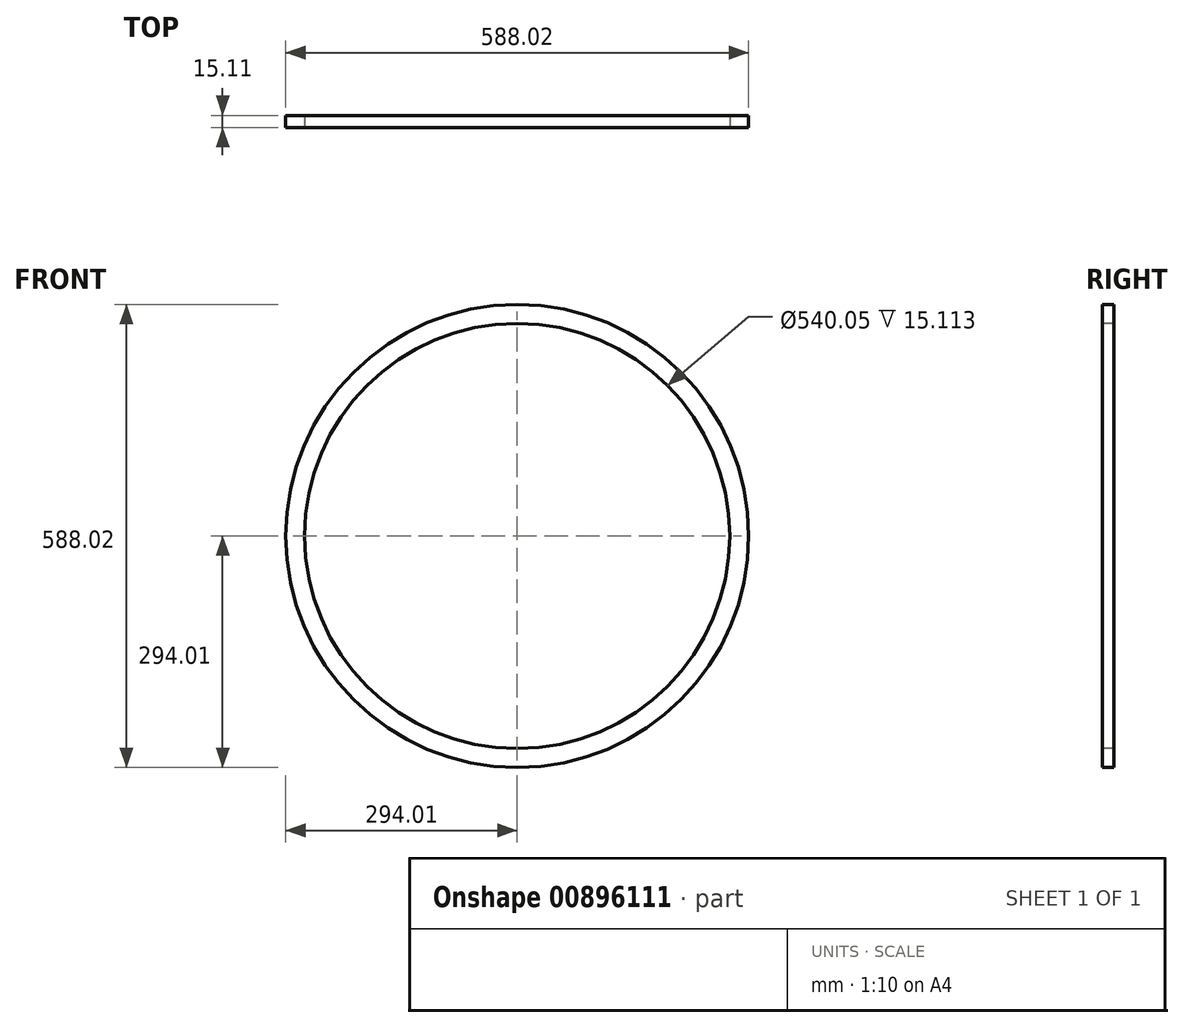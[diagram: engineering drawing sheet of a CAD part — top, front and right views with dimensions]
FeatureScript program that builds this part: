
annotation { "Feature Type Name" : "Feature", "Feature Type Description" : "" }
export const myFeature = defineFeature(function(context is Context, id is Id, definition is map)
    precondition{}
    {
        {
            var Q0;
            Q0=qCreatedBy(makeId("Front.planeOp"),FACE);
            var sketch = newSketch(context, id + "F0", { "sketchPlane" : qUnion([Q0])});
            skCircle(sketch, "E0", {"center": v(0, 0) * mm, "radius": 294 * mm});
            skCircle(sketch, "E1", {"center": v(0, 0) * mm, "radius": 270.03 * mm});
            skSolve(sketch);
        }
        {
            var Q0;
            Q0=makeQuery(id+"F0.imprint","IMPRINT",FACE,{"disambiguationData":[TD([[makeQuery(id+"F0.imprint","IMPRINT",EDGE,{"derivedFrom":sQuery(id+"F0.wireOp",EDGE,"E0")}),1.0]])]});
            extrude(context, id + "F1", {"entities" : qUnion([Q0]), "oppositeDirection" : true, "depth" : (.595 * 25.4) * mm, "offsetDistance" : 25 * mm});
        }
    });
